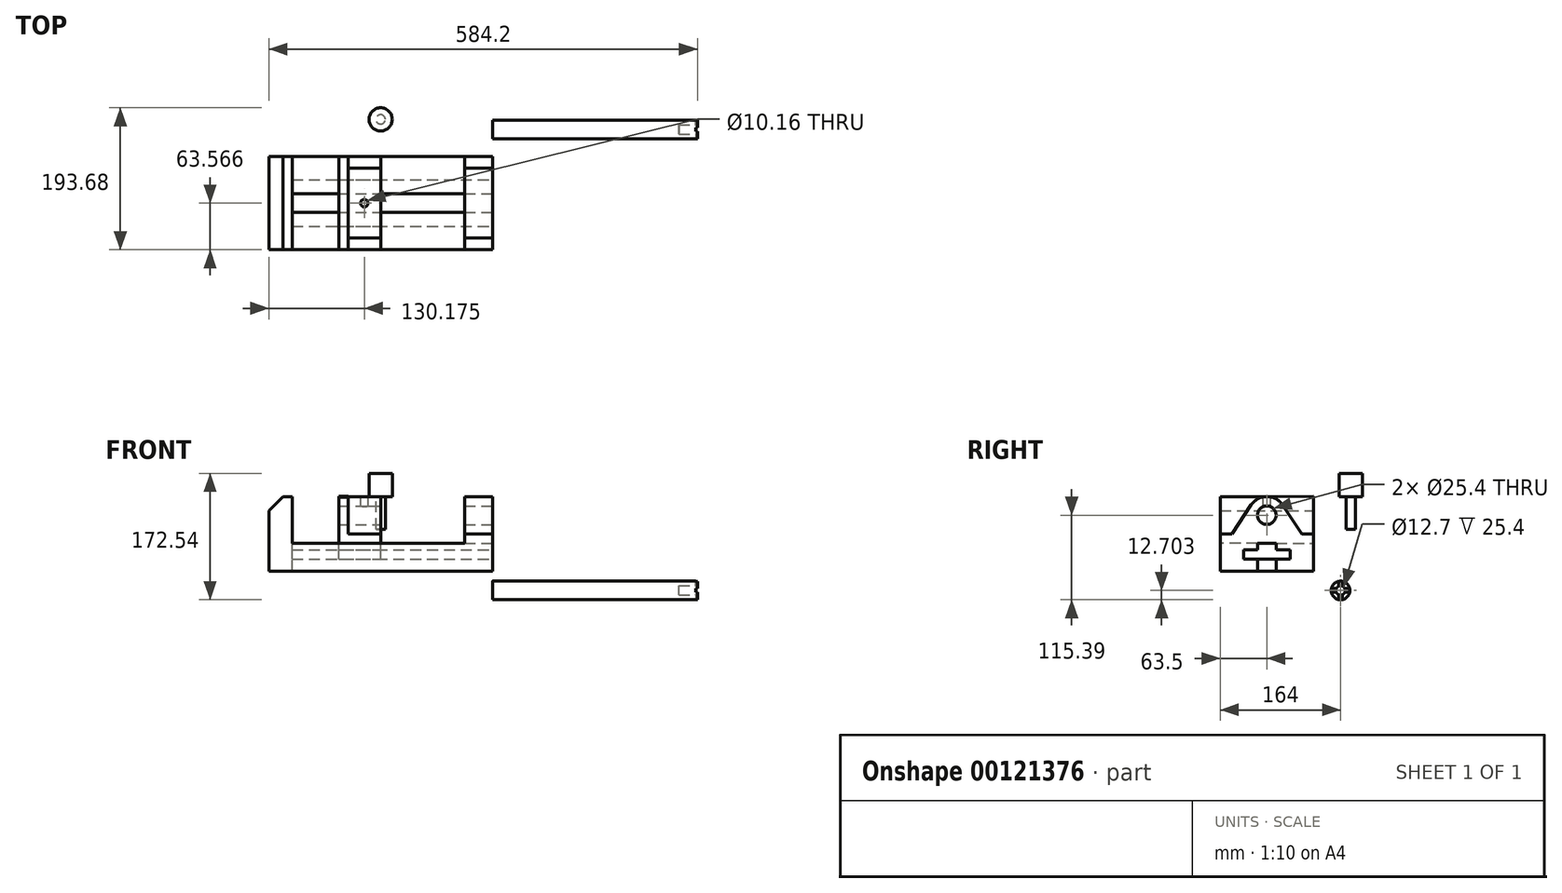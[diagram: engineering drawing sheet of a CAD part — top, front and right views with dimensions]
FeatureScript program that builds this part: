
annotation { "Feature Type Name" : "Feature", "Feature Type Description" : "" }
export const myFeature = defineFeature(function(context is Context, id is Id, definition is map)
    precondition{}
    {
        {
            var Q0;
            Q0=qCreatedBy(makeId("Front.planeOp"),FACE);
            var sketch = newSketch(context, id + "F0", { "sketchPlane" : qUnion([Q0])});
            skLineSegment(sketch, "E0", {"start": v(-152.4, 0) * mm, "end": v(152.4, 0) * mm});
            skLineSegment(sketch, "E1", {"start": v(152.4, 0) * mm, "end": v(152.4, 101.6) * mm});
            skLineSegment(sketch, "E2", {"start": v(152.4, 101.6) * mm, "end": v(114.3, 101.6) * mm});
            skLineSegment(sketch, "E3", {"start": v(114.3, 101.6) * mm, "end": v(114.3, 38.1) * mm});
            skLineSegment(sketch, "E4", {"start": v(114.3, 38.1) * mm, "end": v(-120.65, 38.1) * mm});
            skLineSegment(sketch, "E5", {"start": v(-120.65, 38.1) * mm, "end": v(-120.65, 101.6) * mm});
            skLineSegment(sketch, "E6", {"start": v(-120.65, 101.6) * mm, "end": v(-133.35, 101.6) * mm});
            skLineSegment(sketch, "E7", {"start": v(-133.35, 101.6) * mm, "end": v(-152.4, 82.55) * mm});
            skLineSegment(sketch, "E8", {"start": v(-152.4, 82.55) * mm, "end": v(-152.4, 0) * mm});
            skSolve(sketch);
        }
        {
            var Q0;
            Q0=makeQuery(id+"F0.imprint","IMPRINT",FACE,{"disambiguationData":[TD([[makeQuery(id+"F0.imprint","IMPRINT",EDGE,{"derivedFrom":sQuery(id+"F0.wireOp",EDGE,"E0")}),1.0]])]});
            extrude(context, id + "F1", {"entities" : qUnion([Q0]), "depth" : 127 * mm});
        }
        {
            var Q0;
            Q0=makeQuery(id+"F1.opExtrude","SWEPT_FACE",FACE,{"disambiguationData":[OSD([sQuery(id+"F0.wireOp",EDGE,"E1")])]});
            var sketch = newSketch(context, id + "F2", { "sketchPlane" : qUnion([Q0])});
            skLineSegment(sketch, "E9", {"start": v(-127, 0) * mm, "end": v(-127, 50.8) * mm});
            skLineSegment(sketch, "E10", {"start": v(-127, 50.8) * mm, "end": v(-111.13, 50.8) * mm});
            skLineSegment(sketch, "E11", {"start": v(-127, 0) * mm, "end": v(0, 0) * mm});
            skLineSegment(sketch, "E12", {"start": v(0, 0) * mm, "end": v(0, 50.8) * mm});
            skLineSegment(sketch, "E13", {"start": v(0, 50.8) * mm, "end": v(-15.88, 50.8) * mm});
            skLineSegment(sketch, "E14", {"start": v(-76.2, 0) * mm, "end": v(-76.2, 16.51) * mm});
            skLineSegment(sketch, "E15", {"start": v(-76.2, 16.51) * mm, "end": v(-95.25, 16.51) * mm});
            skLineSegment(sketch, "E16", {"start": v(-95.25, 16.51) * mm, "end": v(-95.25, 29.21) * mm});
            skLineSegment(sketch, "E17", {"start": v(-95.25, 29.2) * mm, "end": v(-76.2, 29.2) * mm});
            skLineSegment(sketch, "E18", {"start": v(-76.2, 29.21) * mm, "end": v(-76.2, 38.1) * mm});
            skLineSegment(sketch, "E19", {"start": v(-76.2, 38.1) * mm, "end": v(-50.8, 38.1) * mm});
            skLineSegment(sketch, "E20", {"start": v(-50.8, 38.1) * mm, "end": v(-50.8, 29.21) * mm});
            skLineSegment(sketch, "E21", {"start": v(-50.8, 29.2) * mm, "end": v(-31.75, 29.21) * mm});
            skLineSegment(sketch, "E22", {"start": v(-31.75, 29.21) * mm, "end": v(-31.75, 16.51) * mm});
            skLineSegment(sketch, "E23", {"start": v(-31.75, 16.51) * mm, "end": v(-50.8, 16.51) * mm});
            skLineSegment(sketch, "E24", {"start": v(-50.8, 16.51) * mm, "end": v(-50.8, 0) * mm});
            skLineSegment(sketch, "E25", {"start": v(-50.8, 0) * mm, "end": v(-76.2, 0) * mm});
            skLineSegment(sketch, "E26", {"start": v(-111.13, 50.8) * mm, "end": v(-84.6, 90.35) * mm});
            skLineSegment(sketch, "E27", {"start": v(-15.87, 50.8) * mm, "end": v(-42.4, 90.35) * mm});
            skArc(sketch, "E28", {"start": v(-42.4, 90.35) * mm, "mid": v(-63.5, 101.6) * mm, "end": v(-84.6, 90.35) * mm});
            skCircle(sketch, "E29", {"center": v(-63.5, 76.2) * mm, "radius": 12.7 * mm});
            skLineSegment(sketch, "E30", {"start": v(-63.5, 105.02) * mm, "end": v(-63.5, -6.57) * mm, "construction": true});
            skPoint(sketch, "E30.startSnap0", {"position": v(-63.5, 101.6) * mm});
            skPoint(sketch, "E30.endSnap0", {"position": v(-63.5, 0) * mm});
            skSolve(sketch);
        }
        {
            var Q0;
            Q0=makeQuery(id+"F2.imprint","IMPRINT",FACE,{"disambiguationData":[TD([[makeQuery(id+"F2.imprint","IMPRINT",EDGE,{"derivedFrom":sQuery(id+"F2.wireOp",EDGE,"E14")}),-1.0]])]});
            var Q1;
            Q1=makeQuery(id+"F1.opExtrude","SWEPT_FACE",FACE,{"disambiguationData":[OSD([sQuery(id+"F0.wireOp",EDGE,"E5")])]});
            extrude(context, id + "F3", {"entities" : qUnion([Q0]), "operationType" : NewBodyOperationType.REMOVE, "endBound" : BoundingType.UP_TO_SURFACE, "oppositeDirection" : true, "endBoundEntityFace" : qUnion([Q1]), "depth" : 25.4 * mm});
        }
        {
            var Q0;
            {var subQ7=sQuery(id+"F2.wireOp",EDGE,"E10");Q0=makeQuery(id+"F2.imprint","IMPRINT",FACE,{"disambiguationData":[TD([[makeQuery(id+"F2.imprint","IMPRINT",EDGE,{"derivedFrom":subQ7}),1.0]])]});}
            var Q1;
            {var subQ4=sQuery(id+"F2.wireOp",EDGE,"E13");Q1=makeQuery(id+"F2.imprint","IMPRINT",FACE,{"disambiguationData":[TD([[makeQuery(id+"F2.imprint","IMPRINT",EDGE,{"derivedFrom":subQ4}),-1.0]])]});}
            var Q2;
            Q2=makeQuery(id+"F2.imprint","IMPRINT",FACE,{"disambiguationData":[TD([[makeQuery(id+"F2.imprint","IMPRINT",EDGE,{"derivedFrom":sQuery(id+"F2.wireOp",EDGE,"E29")}),1.0]])]});
            extrude(context, id + "F4", {"entities" : qUnion([Q0, Q1, Q2]), "operationType" : NewBodyOperationType.REMOVE, "endBound" : BoundingType.UP_TO_NEXT, "oppositeDirection" : true, "depth" : 25.4 * mm});
        }
        {
            var Q0;
            Q0=qCreatedBy(makeId("Right.planeOp"),FACE);
            var sketch = newSketch(context, id + "F5", { "sketchPlane" : qUnion([Q0])});
            skLineSegment(sketch, "E31", {"start": v(-95.25, 16.51) * mm, "end": v(-31.75, 16.51) * mm});
            skLineSegment(sketch, "E32", {"start": v(-31.75, 16.51) * mm, "end": v(-31.75, 29.21) * mm});
            skLineSegment(sketch, "E33", {"start": v(-31.75, 29.21) * mm, "end": v(-50.8, 29.21) * mm});
            skLineSegment(sketch, "E34", {"start": v(-50.8, 29.21) * mm, "end": v(-50.8, 38.1) * mm});
            skLineSegment(sketch, "E35", {"start": v(-95.25, 16.51) * mm, "end": v(-95.25, 29.2) * mm});
            skLineSegment(sketch, "E36", {"start": v(-95.25, 29.2) * mm, "end": v(-76.2, 29.2) * mm});
            skLineSegment(sketch, "E37", {"start": v(-76.2, 29.2) * mm, "end": v(-76.2, 38.1) * mm});
            skLineSegment(sketch, "E38", {"start": v(-76.2, 38.1) * mm, "end": v(-127, 38.1) * mm});
            skLineSegment(sketch, "E39", {"start": v(-127, 38.1) * mm, "end": v(-127, 50.8) * mm});
            skLineSegment(sketch, "E40", {"start": v(-127, 50.8) * mm, "end": v(-111.13, 50.8) * mm});
            skLineSegment(sketch, "E41", {"start": v(-111.13, 50.8) * mm, "end": v(-84.6, 90.35) * mm});
            skLineSegment(sketch, "E42", {"start": v(-50.8, 38.1) * mm, "end": v(0, 38.1) * mm});
            skLineSegment(sketch, "E43", {"start": v(0, 38.1) * mm, "end": v(0, 50.8) * mm});
            skLineSegment(sketch, "E44", {"start": v(0, 50.8) * mm, "end": v(-15.87, 50.8) * mm});
            skLineSegment(sketch, "E45", {"start": v(-15.87, 50.8) * mm, "end": v(-42.4, 90.35) * mm});
            skArc(sketch, "E46", {"start": v(-42.4, 90.35) * mm, "mid": v(-63.5, 101.6) * mm, "end": v(-84.6, 90.35) * mm});
            skCircle(sketch, "E47", {"center": v(-63.5, 76.2) * mm, "radius": 12.7 * mm});
            skLineSegment(sketch, "E48", {"start": v(-127, 50.8) * mm, "end": v(-127, 101.02) * mm});
            skLineSegment(sketch, "E49", {"start": v(-127, 101.02) * mm, "end": v(-63.5, 101.6) * mm});
            skPoint(sketch, "E49.endSnap0", {"position": v(-63.5, 101.6) * mm});
            skLineSegment(sketch, "E50", {"start": v(-63.5, 101.6) * mm, "end": v(0, 102.18) * mm});
            skLineSegment(sketch, "E51", {"start": v(0, 102.18) * mm, "end": v(0, 50.8) * mm});
            skSolve(sketch);
        }
        {
            var Q0;
            Q0=makeQuery(id+"F5.imprint","IMPRINT",FACE,{"disambiguationData":[TD([[makeQuery(id+"F5.imprint","IMPRINT",EDGE,{"derivedFrom":sQuery(id+"F5.wireOp",EDGE,"E31")}),1.0]])]});
            var Q1;
            Q1=makeQuery(id+"F5.imprint","IMPRINT",FACE,{"disambiguationData":[TD([[makeQuery(id+"F5.imprint","IMPRINT",EDGE,{"derivedFrom":sQuery(id+"F5.wireOp",EDGE,"E40")}),1.0]])]});
            var Q2;
            Q2=makeQuery(id+"F5.imprint","IMPRINT",FACE,{"disambiguationData":[TD([[makeQuery(id+"F5.imprint","IMPRINT",EDGE,{"derivedFrom":sQuery(id+"F5.wireOp",EDGE,"E44")}),-1.0]])]});
            extrude(context, id + "F6", {"entities" : qUnion([Q0, Q1, Q2]), "oppositeDirection" : true, "depth" : 57.15 * mm});
        }
        {
            var Q0;
            Q0=makeQuery(id+"F5.imprint","IMPRINT",FACE,{"disambiguationData":[TD([[makeQuery(id+"F5.imprint","IMPRINT",EDGE,{"derivedFrom":sQuery(id+"F5.wireOp",EDGE,"E40")}),1.0]])]});
            var Q1;
            Q1=makeQuery(id+"F5.imprint","IMPRINT",FACE,{"disambiguationData":[TD([[makeQuery(id+"F5.imprint","IMPRINT",EDGE,{"derivedFrom":sQuery(id+"F5.wireOp",EDGE,"E44")}),-1.0]])]});
            extrude(context, id + "F7", {"entities" : qUnion([Q0, Q1]), "operationType" : NewBodyOperationType.REMOVE, "oppositeDirection" : true, "depth" : 44.45 * mm});
        }
        {
            var Q0;
            Q0=makeQuery(id+"F6.opExtrude","SWEPT_FACE",FACE,{"disambiguationData":[OSD([sQuery(id+"F5.wireOp",EDGE,"E49"),sQuery(id+"F5.wireOp",EDGE,"E50")])]});
            var sketch = newSketch(context, id + "F8", { "sketchPlane" : qUnion([Q0])});
            skLineSegment(sketch, "E52", {"start": v(0, -62.56) * mm, "end": v(-72.37, -62.56) * mm, "construction": true});
            skCircle(sketch, "E53", {"center": v(-22.23, -62.56) * mm, "radius": 5.08 * mm});
            skSolve(sketch);
        }
        {
            var Q0;
            Q0=makeQuery(id+"F8.imprint","IMPRINT",FACE,{"disambiguationData":[TD([[makeQuery(id+"F8.imprint","IMPRINT",EDGE,{"derivedFrom":sQuery(id+"F8.wireOp",EDGE,"E53")}),1.0]])]});
            var Q1;
            Q1=sQuery(id+"F8.wireOp",EDGE,"E53");
            extrude(context, id + "F9", {"entities" : qUnion([Q0]), "operationType" : NewBodyOperationType.REMOVE, "surfaceEntities" : qUnion([Q1]), "oppositeDirection" : true, "depth" : 25.4 * mm});
        }
        {
            var Q0;
            {var subQ2=sQuery(id+"F2.wireOp",EDGE,"E9");Q0=makeQuery(id+"F2.imprint","IMPRINT",FACE,{"disambiguationData":[TD([[makeQuery(id+"F2.imprint","IMPRINT",EDGE,{"derivedFrom":subQ2}),-1.0]])]});}
            var sketch = newSketch(context, id + "F10", { "sketchPlane" : qUnion([Q0])});
            skLineSegment(sketch, "E54", {"start": v(0, 0) * mm, "end": v(37, 0) * mm, "construction": true});
            skLineSegment(sketch, "E55", {"start": v(37, 0) * mm, "end": v(37, -52.97) * mm, "construction": true});
            skCircle(sketch, "E56", {"center": v(37, -26.49) * mm, "radius": 12.7 * mm});
            skSolve(sketch);
        }
        {
            var Q0;
            Q0=makeQuery(id+"F10.imprint","IMPRINT",FACE,{"disambiguationData":[TD([[makeQuery(id+"F10.imprint","IMPRINT",EDGE,{"derivedFrom":sQuery(id+"F10.wireOp",EDGE,"E56")}),1.0]])]});
            extrude(context, id + "F11", {"entities" : qUnion([Q0]), "depth" : 279.4 * mm});
        }
        {
            var Q0;
            Q0=makeQuery(id+"F11.opExtrude","CAP_FACE",FACE,{"disambiguationData":[OSD([sQuery(id+"F10.wireOp",EDGE,"E56")])],"isStart":false});
            var sketch = newSketch(context, id + "F12", { "sketchPlane" : qUnion([Q0])});
            skCircle(sketch, "E57", {"center": v(37, -26.49) * mm, "radius": 6.35 * mm});
            skLineSegment(sketch, "E58", {"start": v(34.46, -20.67) * mm, "end": v(34.46, -14.04) * mm});
            skLineSegment(sketch, "E59", {"start": v(39.54, -20.67) * mm, "end": v(39.54, -14.04) * mm});
            skLineSegment(sketch, "E60", {"start": v(34.46, -32.3) * mm, "end": v(34.46, -38.93) * mm});
            skLineSegment(sketch, "E61", {"start": v(39.54, -32.3) * mm, "end": v(39.54, -38.93) * mm});
            skLineSegment(sketch, "E62", {"start": v(42.82, -23.95) * mm, "end": v(49.44, -23.95) * mm});
            skLineSegment(sketch, "E63", {"start": v(42.82, -29.03) * mm, "end": v(49.44, -29.03) * mm});
            skLineSegment(sketch, "E64", {"start": v(31.18, -23.95) * mm, "end": v(24.56, -23.95) * mm});
            skLineSegment(sketch, "E65", {"start": v(31.18, -29.03) * mm, "end": v(24.56, -29.03) * mm});
            skSolve(sketch);
        }
        {
            var Q0;
            {var subQ0=sQuery(id+"F12.wireOp",EDGE,"E57");var subQ4=makeQuery(id+"F12.imprint","INTERSECT",VERTEX,{"derivedFrom":[subQ0,sQuery(id+"F12.wireOp",EDGE,"E59")]});Q0=makeQuery(id+"F12.imprint","IMPRINT",FACE,{"disambiguationData":[TD([[makeQuery(id+"F12.imprint","IMPRINT",EDGE,{"disambiguationData":[TD([[subQ4,1.0]])],"derivedFrom":subQ0}),1.0]])]});}
            var Q1;
            Q1=sQuery(id+"F12.wireOp",EDGE,"E57");
            extrude(context, id + "F13", {"entities" : qUnion([Q0]), "operationType" : NewBodyOperationType.REMOVE, "surfaceEntities" : qUnion([Q1]), "oppositeDirection" : true, "depth" : 25.4 * mm});
        }
        {
            var Q0;
            {var subQ0=sQuery(id+"F12.wireOp",EDGE,"E64");Q0=makeQuery(id+"F12.imprint","IMPRINT",FACE,{"disambiguationData":[TD([[makeQuery(id+"F12.imprint","IMPRINT",EDGE,{"derivedFrom":subQ0}),1.0]])]});}
            var Q1;
            {var subQ0=sQuery(id+"F12.wireOp",EDGE,"E58");Q1=makeQuery(id+"F12.imprint","IMPRINT",FACE,{"disambiguationData":[TD([[makeQuery(id+"F12.imprint","IMPRINT",EDGE,{"derivedFrom":subQ0}),-1.0]])]});}
            var Q2;
            {var subQ0=sQuery(id+"F12.wireOp",EDGE,"E62");Q2=makeQuery(id+"F12.imprint","IMPRINT",FACE,{"disambiguationData":[TD([[makeQuery(id+"F12.imprint","IMPRINT",EDGE,{"derivedFrom":subQ0}),-1.0]])]});}
            var Q3;
            {var subQ0=sQuery(id+"F12.wireOp",EDGE,"E60");Q3=makeQuery(id+"F12.imprint","IMPRINT",FACE,{"disambiguationData":[TD([[makeQuery(id+"F12.imprint","IMPRINT",EDGE,{"derivedFrom":subQ0}),1.0]])]});}
            extrude(context, id + "F14", {"entities" : qUnion([Q0, Q1, Q2, Q3]), "operationType" : NewBodyOperationType.REMOVE, "oppositeDirection" : true, "depth" : 2.54 * mm});
        }
        {
            var Q0;
            Q0=makeQuery(id+"F1.opExtrude","SWEPT_FACE",FACE,{"disambiguationData":[OSD([sQuery(id+"F0.wireOp",EDGE,"E6")])]});
            var sketch = newSketch(context, id + "F15", { "sketchPlane" : qUnion([Q0])});
            skCircle(sketch, "E66", {"center": v(0, 50.8) * mm, "radius": 15.88 * mm});
            skSolve(sketch);
        }
        {
            var Q0;
            Q0=makeQuery(id+"F15.imprint","IMPRINT",FACE,{"disambiguationData":[TD([[makeQuery(id+"F15.imprint","IMPRINT",EDGE,{"derivedFrom":sQuery(id+"F15.wireOp",EDGE,"E66")}),1.0]])]});
            extrude(context, id + "F16", {"entities" : qUnion([Q0]), "depth" : 31.75 * mm});
        }
        {
            var Q0;
            Q0=makeQuery(id+"F16.opExtrude","CAP_FACE",FACE,{"disambiguationData":[OSD([sQuery(id+"F15.wireOp",EDGE,"E66")])],"isStart":true});
            var sketch = newSketch(context, id + "F17", { "sketchPlane" : qUnion([Q0])});
            skCircle(sketch, "E67", {"center": v(0, -50.8) * mm, "radius": 6.35 * mm});
            skSolve(sketch);
        }
        {
            var Q0;
            Q0=makeQuery(id+"F17.imprint","IMPRINT",FACE,{"disambiguationData":[TD([[makeQuery(id+"F17.imprint","IMPRINT",EDGE,{"derivedFrom":sQuery(id+"F17.wireOp",EDGE,"E67")}),1.0]])]});
            var Q1;
            Q1=sQuery(id+"F17.wireOp",EDGE,"E67");
            extrude(context, id + "F18", {"entities" : qUnion([Q0]), "operationType" : NewBodyOperationType.ADD, "surfaceEntities" : qUnion([Q1]), "depth" : 44.45 * mm});
        }
    });
